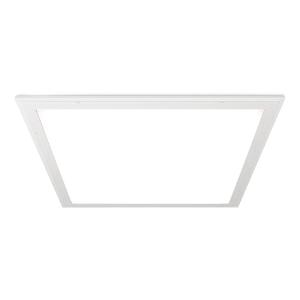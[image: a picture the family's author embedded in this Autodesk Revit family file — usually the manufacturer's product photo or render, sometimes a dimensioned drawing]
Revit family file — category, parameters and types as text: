
# Revit family: 3f_filippi_-_l_650_luce_diffusa_lgs_3f_filippi_-_21875_-_l_650_52w-940_dali_ep_lgs_596x596
name_source: partatom
category: Lighting Fixtures
units: mm (PartAtom-declared; Revit-internal decimal feet)

## family parameters
Cut with Voids When Loaded = No
Host = Face
Light Source = No
Part Type = Normal
Room Calculation Point = No
Round Connector Dimension = Use Diameter
Shared = No

## types (1)
- 3F Filippi - L 650 Luce Diffusa LGS (1 x LED, 5551 lm, 58 W, 4000 K)
    Apparent Load = 58 VA
    Approval mark = ENEC
    CIE Flux Codes = 66 93 98 100 100
    Color Rendering = 90
    Color Temperature = 4000 K
    Control Gear = Electronic ballast
    Default Elevation = 1800 mm
    Description = ILLUMINOTECHNICAL
Luminous efficiency 100% (DLOR 100%, ULOR 0%).
Initial luminous flux of the luminaire 5551 lm.
Emergency luminaire luminous flux BLF 10.9%.
Direct symmetric distribution.
Installation Interdistance Transv.D = 1.14 x hu - Long.D = 1.16 x hu.
Average luminance <3000 cd/m² for radial angles >65°.
Tabular UGR (CIE 117 - 4H-8H; S=0.25H; 70/50/20): RUG 18.2 - 18.1.
Beam angle: 85° - 85°.
Luminous efficacy 96 lm/W.
Lifetime (L93/B10): 30000 h. (tq+25°C)
Lifetime (L90/B10): 50000 h. (tq+25°C)
Lifetime (L85/B10): 80000 h. (tq+25°C)
Lifetime (L80/B10): 100000 h. (tq+25°C)
Sudden decreased luminous flux after 50000 hours: 0% (C0).
Photobiological safety in compliance with IEC/TR 62778: RG0 risk exempt, (IEC 62471).
In compliance with IEC/EN 62722-2-1 - IEC/EN 62717 standards.

SOURCE
Squared LED module 52W/940.
Source with special protection against aggressive chemically-volatile substances for standard LED technology.
Energy efficiency class (UE 2019/2020 - UE 2019/2015): E.
CIE 13.3 Colour rendering index: CRI >90 (R9 >50%).
IES TM-30 Fidelity Index: Rf = 92 Rg = 101.
CCT nominal colour temperature 4000 K.
Colour initial tolerance (MacAdam): SDCM 3.

MECHANICAL
Housing in galvannealed steel, painted in white epoxy-polyester.
Perimetral frame in white stainless steel.
LGS micro-prismatic flat diffuser in transparent methacrylate (PMMA), multi-lenticular exterior, anti-glare.
Anti-glare opal polycarbonate filter for brightness uniformity.
Luminaire with limited surface temperature. - D - (EN 60598-2-24)
Dimensions: 596x596 mm, height 90 mm. Weight 7.6 kg.
IP66 protection degree for exposed part, IP64 for recessed part.
Mechanical strength to impacts IK06 (1 joule).
Glow-wire test resistance 650°C.

ELECTRICAL
Halogen Free DALI-2 DATI (Parts 251, 252, 253), PUSH-DIM, electronic wiring 230V-50/60Hz, power factor 0.95 at full load, THD <25%, constant output current, SELV, class I, 1 driver, 1 DALI addresse.
Power of the luminaire 58 W.
CE - IEC 60598-1 - EN 60598-1.
EP maintained emergency wiring on board with dedicated quick connection, 1h duration, 24h recharge; compliant with EN 60598-2-22, excluding high risk areas.
SAFE FLICKER: PstLM=<1 and SVM=<0.4 (IEC TR 61547-1 and IEC TR 63158), to ensure a more comfortable and safe light.
Ambient temperature from +5°C to +25°C.
Temperature class T6 max 85°C.
5-pole terminal block (L-N-PE-DA/DA) quick connection for line connection with connection capacity 2x2.5 mm² per poles.
Relative humidity UR: <85%.

INSTALLATION
Lay-in recessed fitting.
All accessories dedicated to this product are available on the Catalog and on our website www.3F-Filippi.com.

APPLICATIONS
Suitable product for food production plants (HACCP), IFS (Food Version 6), BRC (GSFS Food Version 7).
Environments: hospital premises, transit areas, laboratories, platform-roof, underpasses.
Environments: sterilized, aseptic.
In hospital environments, food industry or machines with parts in motion, with considerable sudden temperature changes, and in general in any environments requiring total protection against falling fragments, use luminaires with laminated glass only.
Tempered glass is not immune to falling fragments from harmless and caused by shocks or exceptionally derived from the tempering process.
Environments requiring a high level of protection and simplified cleaning.
Environments with exacting visual tasks, where diffused soft light for optimum visual comfort is required.

LIGHT MANAGEMENT
Recommended minimum setting: 10%.
The luminaire, equipped with (DALI-2 DATI) driver, can be controlled manually with 3F Easy Dim technology or automatically/manually with wired or wireless DALI/D2D control systems.
The D2D driver guarantees interoperability with other devices with the same certification by making the following information available:
Device Data (Part 251), Energy Report (Part 252), Diagnosis & Maintenance (Part 253).
In electrical systems without a regulation system (manual or automatic) and DALI bus, a suitable jumper must be made on the DA-DA terminals of the appliance.

WARNING
Luminaire designed for disposal/recycling at end-of-life.
Replaceable (LED only) light source by a professional. Replaceable control gear by a professional.
    Height = 0 mm  [stored 0 ft]
    Lamp = 1 x LED
    Lamp Light Flux = 5551 lm
    Lamp Power = 58 W
    Lamp count = 1
    Length = 596 mm
    Lifetime = 50000 h
    Luminous efficacy = 96 lm/W
    Manufacturer = 3F Filippi
    ModVariant = No
    Model = 3F Filippi - 21875 - L 650 52W-940 DALI EP LGS 596x596
    Mounting Place = Ceiling
    Mounting Type = Recessed
    Number of Poles = 1
    OnlyDefault = Yes
    Power Factor = 1
    Product Name = 3F Filippi - L 650 Luce Diffusa LGS
    Product group = recessed luminaire
    ProductGroupID = 4
    Protection Class = Protection class I
    Protection Degree = IP 64
    RLX_Detail_Level = 1
    RLX_Emergency_Light_Flux = 0 lm
    RLX_Emergency_Type = 0
    RLX_Emergency_Type_DB = No
    RlxData = <blob elided: 100489 chars, md5=7a0ad10b>
    Socket = socket
    Standby Power = 0 W
    System Light Flux = 5551 lm
    System Power = 58 W
    Type Comments = Product without accessories
    Type Image = 3ffilippi_l_650_luce_diffusa_lgs.jpg
    URL = http://relux.com
    VarID = ---
    Voltage = 0 V
    Weight = 0.00 kg
    Width = 596 mm

note: [stored X ft] marks values corroborated as IEEE doubles in the binary element streams (Revit-internal decimal feet)

## geometry (parser evidence)
native form markers: Blend x4, Sweep x9
no freeform markers — native parametric forms only
